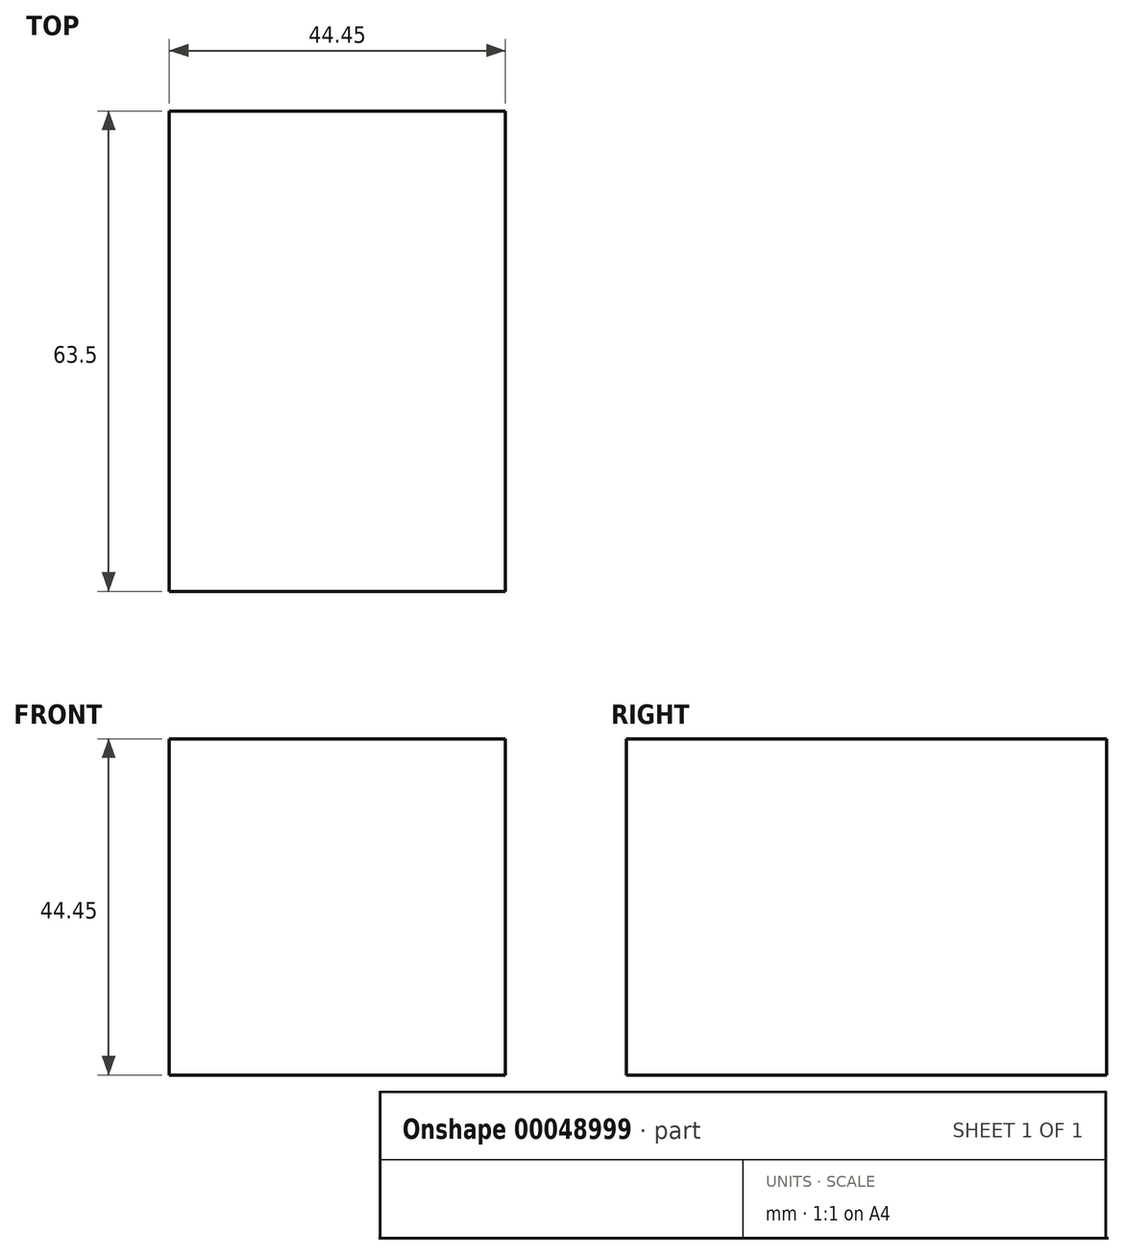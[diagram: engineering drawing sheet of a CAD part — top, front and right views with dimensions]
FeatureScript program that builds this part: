
annotation { "Feature Type Name" : "Feature", "Feature Type Description" : "" }
export const myFeature = defineFeature(function(context is Context, id is Id, definition is map)
    precondition{}
    {
        {
            var Q0;
            Q0=qCreatedBy(makeId("Front.planeOp"),FACE);
            var sketch = newSketch(context, id + "F0", { "sketchPlane" : qUnion([Q0])});
            skLineSegment(sketch, "E0", {"start": v(0, 0) * mm, "end": v(0, 44.45) * mm});
            skLineSegment(sketch, "E1", {"start": v(0, 44.45) * mm, "end": v(44.45, 44.45) * mm});
            skLineSegment(sketch, "E2", {"start": v(44.45, 44.45) * mm, "end": v(44.45, 0) * mm});
            skLineSegment(sketch, "E3", {"start": v(44.45, 0) * mm, "end": v(0, 0) * mm});
            skSolve(sketch);
        }
        {
            var Q0;
            Q0=makeQuery(id+"F0.imprint","IMPRINT",FACE,{"disambiguationData":[TD([[makeQuery(id+"F0.imprint","IMPRINT",EDGE,{"derivedFrom":sQuery(id+"F0.wireOp",EDGE,"E0")}),-1.0]])]});
            extrude(context, id + "F1", {"entities" : qUnion([Q0]), "depth" : 63.5 * mm});
        }
    });
